# Revit family: LSTG 2x2_2x4
name_source: partatom
category: Lighting Fixtures
units: mm (PartAtom-declared; Revit-internal decimal feet)

## family parameters
Always vertical = Yes
Cut with Voids When Loaded = No
Host = Ceiling
Light Source = Yes
OmniClass Number = 23.80.70.11.14.17
OmniClass Title = Direct/Indirect
Part Type = Normal
Room Calculation Point = No
Round Connector Dimension = Use Diameter
Shared = No

## types (5) — shared parameters
Assembly Code = D5020200
Color Filter = 16777215
Description = LED Surface  Type G
Dimming Lamp Color Temperature Shift = <None>
Emit Shape Visible in Rendering = No
Emit from Rectangle Width = 1' - 11 3/4"
Housing Finish = Metal - Viscor - White
Lamp = LED
Lens Finish = Acrylic - Viscor - Frosted White Impact Resistant
Manufacturer = VISIONEERING by VISCOR
Model = LSTG
Reflector Width = 0' - 11 7/8"
Tilt Angle = 90.00°
URL = https://www.viscor.com
Voltage = 120 V
Width = 1' - 11 3/4"

## per-type parameters (varying)
| type | Apparent Load | Emit from Rectangle Length | Lamp Wattage | Length | Photometric Web File |
| LSTG2X2-LED840K037LUNV | 34 VA | 1' - 11 3/4" | 34 VA | 1' - 11 3/4" | LSTG2X2-LED840K037LUNV.IES |
| LSTG2x4-LED840K074LUNV | 58 VA | 3' - 11 3/4" | 58 VA | 3' - 11 3/4" | LSTG2X4-LED840K074LUNV.ies |
| LSTG2x4-LED840K040LUNV | 30 VA | 3' - 11 3/4" | 30 VA | 3' - 11 3/4" | LSTG2x4-LED840K040LUNV.IES |
| LSTG2X2-LED840K050LUNV | 38 VA | 1' - 11 3/4" | 38 VA | 1' - 11 3/4" | LSTG2x2-LED840K050LUNV.IES |
| LSTG2X4-LED840K092LUNV | 79 VA | 3' - 11 3/4" | 79 VA | 3' - 11 3/4" | LSTG2X4-LED840K092LUNV.ies |

## geometry (parser evidence)
native form markers: Sweep x4
no freeform markers — native parametric forms only
